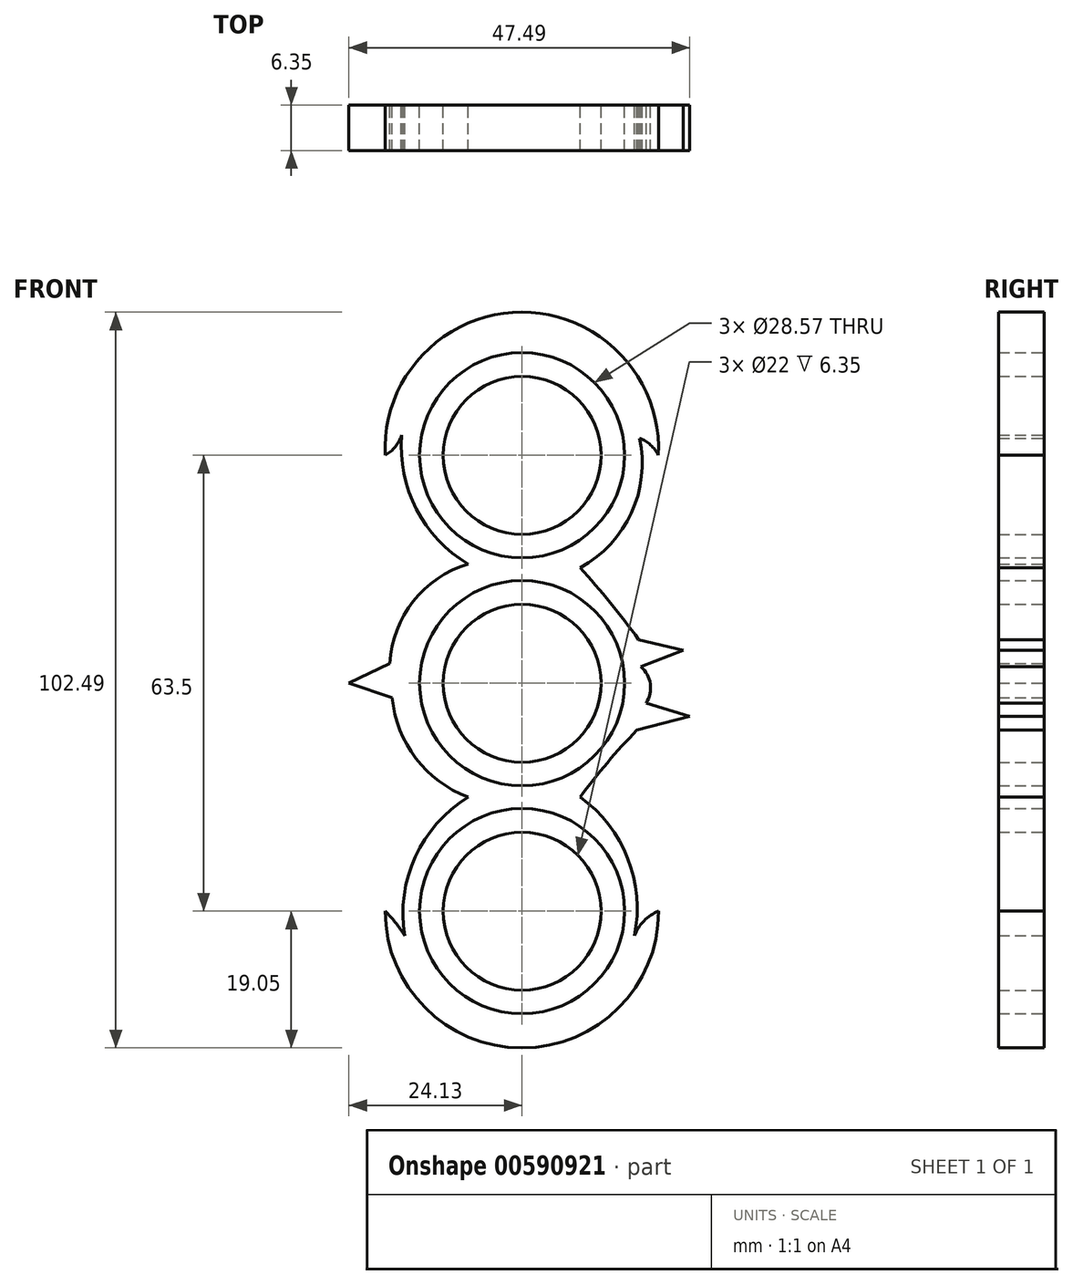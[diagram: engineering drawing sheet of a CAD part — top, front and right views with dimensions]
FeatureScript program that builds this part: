
annotation { "Feature Type Name" : "Feature", "Feature Type Description" : "" }
export const myFeature = defineFeature(function(context is Context, id is Id, definition is map)
    precondition{}
    {
        {
            var Q0;
            Q0=qCreatedBy(makeId("Front.planeOp"),FACE);
            var sketch = newSketch(context, id + "F0", { "sketchPlane" : qUnion([Q0])});
            skCircle(sketch, "E0", {"center": v(0, 0) * mm, "radius": 11 * mm});
            skCircle(sketch, "E1", {"center": v(0, 0) * mm, "radius": 14.29 * mm});
            skCircle(sketch, "E2", {"center": v(0, 31.75) * mm, "radius": 11 * mm});
            skCircle(sketch, "E3", {"center": v(0, 31.75) * mm, "radius": 14.29 * mm});
            skCircle(sketch, "E4.1.0", {"center": v(0, -31.75) * mm, "radius": 11 * mm});
            skCircle(sketch, "E4.1.1", {"center": v(0, -31.75) * mm, "radius": 14.29 * mm});
            skSolve(sketch);
        }
        {
            var Q0;
            Q0=qCreatedBy(makeId("Front.planeOp"),FACE);
            var sketch = newSketch(context, id + "F1", { "sketchPlane" : qUnion([Q0])});
            skCircle(sketch, "E5.0", {"center": v(0, 31.75) * mm, "radius": 14.29 * mm});
            skCircle(sketch, "E6.0", {"center": v(0, 0) * mm, "radius": 14.29 * mm});
            skCircle(sketch, "E7.0", {"center": v(0, -31.75) * mm, "radius": 14.29 * mm});
            skArc(sketch, "E8", {"start": v(18.99, 31.75) * mm, "mid": v(-0.04, 51.7) * mm, "end": v(-19.07, 31.75) * mm});
            skArc(sketch, "E9", {"start": v(-19.07, -31.75) * mm, "mid": v(-0.02, -50.8) * mm, "end": v(19.03, -31.75) * mm});
            skArc(sketch, "E10", {"start": v(19.03, -31.75) * mm, "mid": v(16.99, -33.11) * mm, "end": v(15.65, -35.17) * mm});
            skArc(sketch, "E11", {"start": v(-16.78, 34.54) * mm, "mid": v(-14.73, 24.25) * mm, "end": v(-7.54, 16.6) * mm});
            skArc(sketch, "E12", {"start": v(15.65, -35.17) * mm, "mid": v(14.73, -24.4) * mm, "end": v(8.1, -15.86) * mm});
            skArc(sketch, "E13", {"start": v(-7.54, -15.86) * mm, "mid": v(-14.88, -24.17) * mm, "end": v(-16.35, -35.17) * mm});
            skLineSegment(sketch, "E14", {"start": v(16.25, 6.08) * mm, "end": v(22.43, 4.63) * mm});
            skLineSegment(sketch, "E15", {"start": v(22.43, 4.63) * mm, "end": v(16.53, 2.28) * mm});
            skLineSegment(sketch, "E16", {"start": v(17.28, -2.74) * mm, "end": v(23.36, -4.58) * mm});
            skLineSegment(sketch, "E17", {"start": v(23.36, -4.58) * mm, "end": v(16, -6.55) * mm});
            skLineSegment(sketch, "E18", {"start": v(-18.42, 2.77) * mm, "end": v(-24.13, 0) * mm});
            skLineSegment(sketch, "E19", {"start": v(-24.13, 0) * mm, "end": v(-18.1, -2) * mm});
            skArc(sketch, "E20", {"start": v(16.25, 6.08) * mm, "mid": v(12.3, 11.2) * mm, "end": v(8.1, 16.1) * mm});
            skArc(sketch, "E21", {"start": v(17.28, -2.74) * mm, "mid": v(17.86, -0.08) * mm, "end": v(16.53, 2.28) * mm});
            skArc(sketch, "E22", {"start": v(16, -6.55) * mm, "mid": v(11.88, -11.07) * mm, "end": v(8.1, -15.86) * mm});
            skArc(sketch, "E23", {"start": v(-7.54, 16.6) * mm, "mid": v(-15.18, 11.42) * mm, "end": v(-18.42, 2.77) * mm});
            skArc(sketch, "E24", {"start": v(-18.1, -2) * mm, "mid": v(-14.8, -10.43) * mm, "end": v(-7.54, -15.86) * mm});
            skArc(sketch, "E25", {"start": v(18.99, 31.75) * mm, "mid": v(17.9, 33.18) * mm, "end": v(16.37, 34.13) * mm});
            skArc(sketch, "E26", {"start": v(8.1, 16.1) * mm, "mid": v(15.24, 23.74) * mm, "end": v(16.37, 34.13) * mm});
            skArc(sketch, "E27", {"start": v(-19.07, 31.75) * mm, "mid": v(-17.67, 32.94) * mm, "end": v(-16.78, 34.54) * mm});
            skArc(sketch, "E28", {"start": v(-16.35, -35.17) * mm, "mid": v(-17.6, -33.38) * mm, "end": v(-19.07, -31.75) * mm});
            skSolve(sketch);
        }
        {
            var Q0;
            Q0=makeQuery(id+"F1.imprint","IMPRINT",FACE,{"disambiguationData":[TD([[makeQuery(id+"F1.imprint","IMPRINT",EDGE,{"derivedFrom":sQuery(id+"F1.wireOp",EDGE,"E5.0")}),-1.0]])]});
            var Q1;
            Q1=makeQuery(id+"F0.imprint","IMPRINT",FACE,{"disambiguationData":[TD([[makeQuery(id+"F0.imprint","IMPRINT",EDGE,{"derivedFrom":sQuery(id+"F0.wireOp",EDGE,"E2")}),-1.0]])]});
            var Q2;
            Q2=makeQuery(id+"F0.imprint","IMPRINT",FACE,{"disambiguationData":[TD([[makeQuery(id+"F0.imprint","IMPRINT",EDGE,{"derivedFrom":sQuery(id+"F0.wireOp",EDGE,"E0")}),-1.0]])]});
            var Q3;
            Q3=makeQuery(id+"F0.imprint","IMPRINT",FACE,{"disambiguationData":[TD([[makeQuery(id+"F0.imprint","IMPRINT",EDGE,{"derivedFrom":sQuery(id+"F0.wireOp",EDGE,"E4.1.0")}),-1.0]])]});
            extrude(context, id + "F2", {"entities" : qUnion([Q0, Q1, Q2, Q3]), "depth" : 6.35 * mm, "offsetDistance" : 25.4 * mm});
        }
    });
